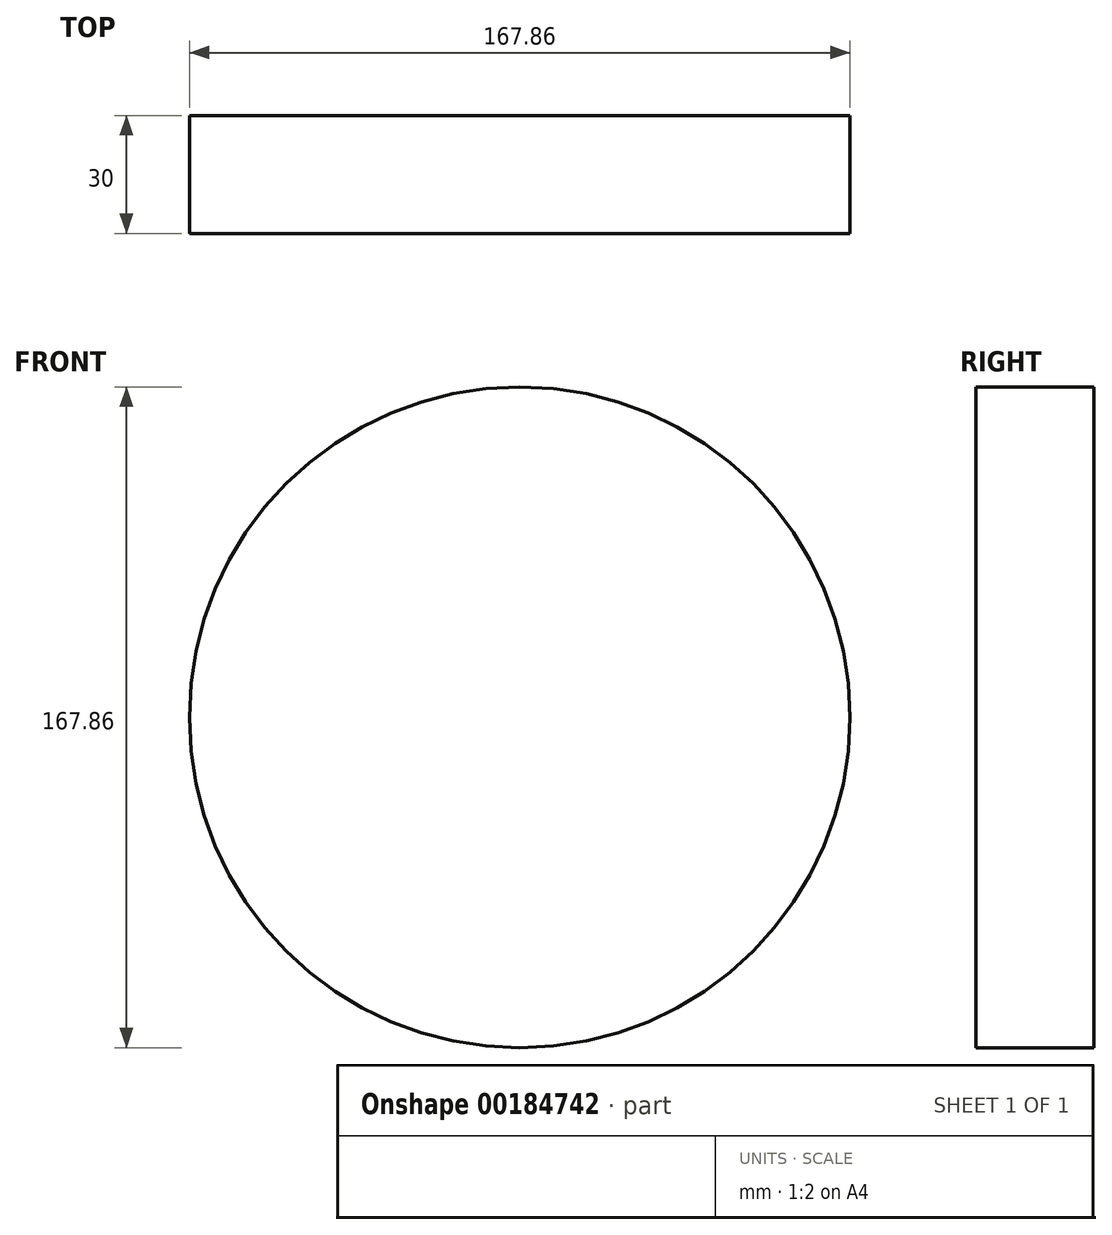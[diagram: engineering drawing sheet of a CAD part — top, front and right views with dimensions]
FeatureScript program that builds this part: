
annotation { "Feature Type Name" : "Feature", "Feature Type Description" : "" }
export const myFeature = defineFeature(function(context is Context, id is Id, definition is map)
    precondition{}
    {
        {
            var Q0;
            Q0=qCreatedBy(makeId("Front.planeOp"),FACE);
            var sketch = newSketch(context, id + "F0", { "sketchPlane" : qUnion([Q0])});
            skEllipse(sketch, "E0", {"center": v(0, 0) * mm, "majorRadius": 72.29 * mm, "minorRadius": 50.5 * mm, "majorAxis": v(1, 0)});
            skSolve(sketch);
        }
        {
            var Q0;
            Q0=makeQuery(id+"F0.imprint","IMPRINT",FACE,{"disambiguationData":[TD([[makeQuery(id+"F0.imprint","IMPRINT",EDGE,{"derivedFrom":sQuery(id+"F0.wireOp",EDGE,"E0")}),1.0]])]});
            extrude(context, id + "F1", {"entities" : qUnion([Q0]), "endBound" : BoundingType.SYMMETRIC, "depth" : 10 * mm});
        }
        {
            var Q0;
            Q0=qCreatedBy(makeId("Front.planeOp"),FACE);
            var sketch = newSketch(context, id + "F2", { "sketchPlane" : qUnion([Q0])});
            skCircle(sketch, "E1", {"center": v(0, 0) * mm, "radius": 83.93 * mm});
            skSolve(sketch);
        }
        {
            var Q0;
            Q0 = qSketchRegion(id + "F2", true);
            extrude(context, id + "F3", {"entities" : qUnion([Q0]), "operationType" : NewBodyOperationType.ADD, "endBound" : BoundingType.SYMMETRIC, "depth" : 30 * mm});
        }
    });
